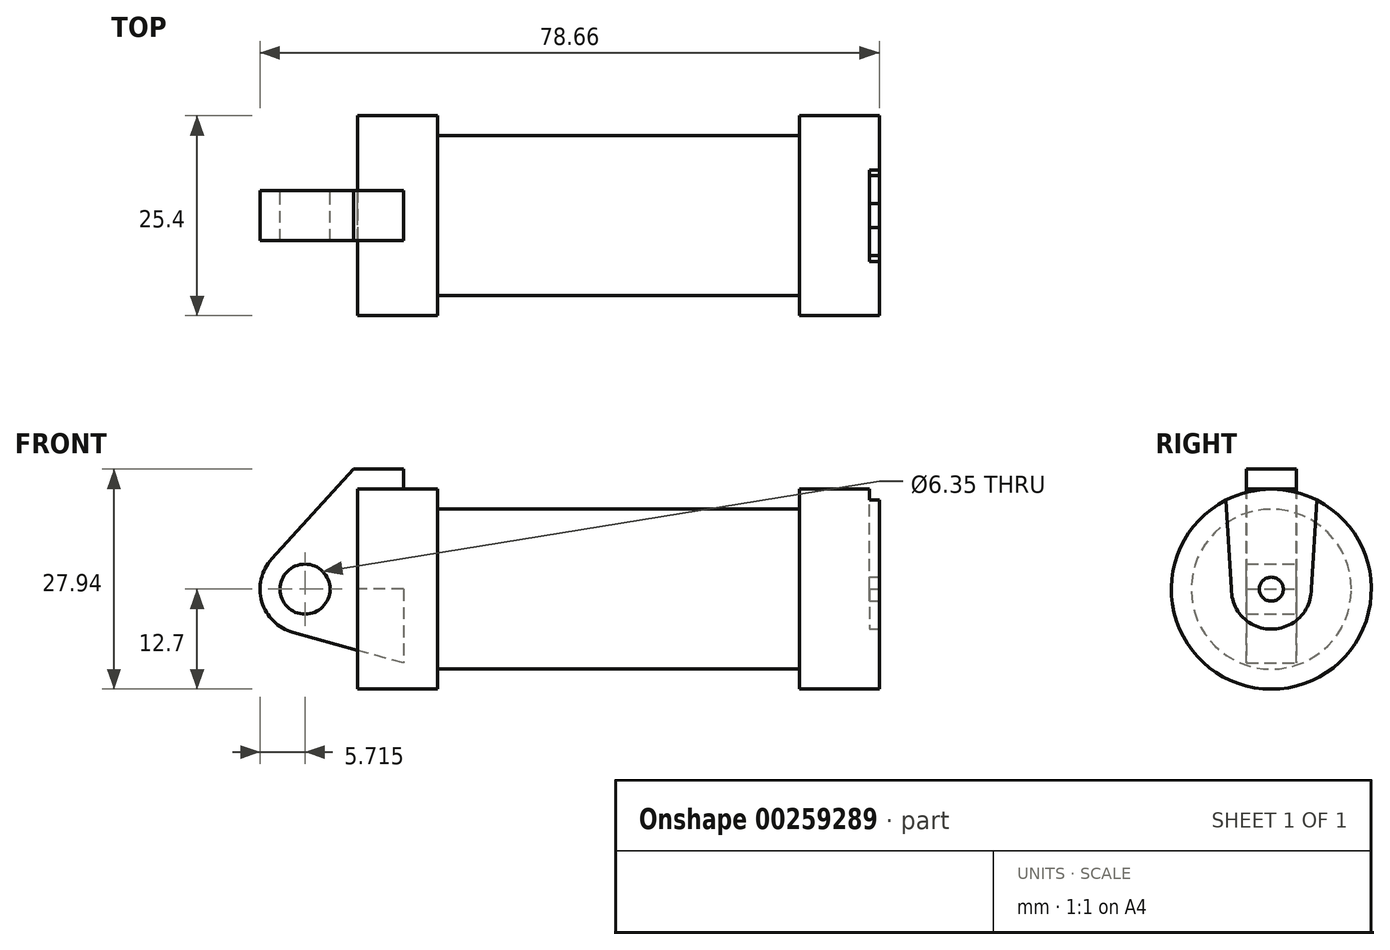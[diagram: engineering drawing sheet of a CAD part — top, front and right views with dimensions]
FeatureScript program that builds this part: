
annotation { "Feature Type Name" : "Feature", "Feature Type Description" : "" }
export const myFeature = defineFeature(function(context is Context, id is Id, definition is map)
    precondition{}
    {
        {
            var Q0;
            Q0=qCreatedBy(makeId("Front.planeOp"),FACE);
            var sketch = newSketch(context, id + "F0", { "sketchPlane" : qUnion([Q0])});
            skLineSegment(sketch, "E0", {"start": v(0, 0) * mm, "end": v(0, 12.7) * mm});
            skLineSegment(sketch, "E1", {"start": v(0, 12.7) * mm, "end": v(10.16, 12.7) * mm});
            skLineSegment(sketch, "E2", {"start": v(10.16, 12.7) * mm, "end": v(10.16, 10.16) * mm});
            skLineSegment(sketch, "E3", {"start": v(10.16, 10.16) * mm, "end": v(56.13, 10.16) * mm});
            skLineSegment(sketch, "E4", {"start": v(56.13, 10.16) * mm, "end": v(56.13, 12.7) * mm});
            skLineSegment(sketch, "E5", {"start": v(56.13, 12.7) * mm, "end": v(66.3, 12.7) * mm});
            skLineSegment(sketch, "E6", {"start": v(66.3, 12.7) * mm, "end": v(66.3, 0) * mm});
            skLineSegment(sketch, "E7", {"start": v(66.3, 0) * mm, "end": v(0, 0) * mm});
            skLineSegment(sketch, "E8", {"start": v(5.84, 15.24) * mm, "end": v(-0.5, 15.24) * mm});
            skLineSegment(sketch, "E9", {"start": v(-0.5, 15.24) * mm, "end": v(-10.88, 3.85) * mm});
            skLineSegment(sketch, "E10", {"start": v(0, 0) * mm, "end": v(-6.65, 0) * mm});
            skCircle(sketch, "E11", {"center": v(-6.65, 0) * mm, "radius": 5.72 * mm});
            skCircle(sketch, "E12", {"center": v(-6.65, 0) * mm, "radius": 3.18 * mm});
            skLineSegment(sketch, "E13", {"start": v(5.84, 15.24) * mm, "end": v(5.84, -9.4) * mm});
            skLineSegment(sketch, "E14", {"start": v(5.84, -9.4) * mm, "end": v(-8.18, -5.5) * mm});
            skSolve(sketch);
        }
        {
            var Q0;
            {var subQ3=sQuery(id+"F0.wireOp",EDGE,"E0");Q0=makeQuery(id+"F0.imprint","IMPRINT",FACE,{"disambiguationData":[TD([[makeQuery(id+"F0.imprint","IMPRINT",EDGE,{"derivedFrom":subQ3}),1.0]])]});}
            var Q1;
            {var subQ0=sQuery(id+"F0.wireOp",EDGE,"E14");Q1=makeQuery(id+"F0.imprint","IMPRINT",FACE,{"disambiguationData":[TD([[makeQuery(id+"F0.imprint","IMPRINT",EDGE,{"derivedFrom":subQ0}),-1.0]])]});}
            var Q2;
            {var subQ4=sQuery(id+"F0.wireOp",EDGE,"E12");Q2=makeQuery(id+"F0.imprint","IMPRINT",FACE,{"disambiguationData":[TD([[makeQuery(id+"F0.imprint","IMPRINT",EDGE,{"derivedFrom":subQ4}),-1.0]])]});}
            extrude(context, id + "F1", {"entities" : qUnion([Q0, Q1, Q2]), "endBound" : BoundingType.SYMMETRIC, "depth" : 6.35 * mm});
        }
        {
            var Q0;
            {var subQ0=sQuery(id+"F0.wireOp",EDGE,"E0");Q0=makeQuery(id+"F0.imprint","IMPRINT",FACE,{"disambiguationData":[TD([[makeQuery(id+"F0.imprint","IMPRINT",EDGE,{"derivedFrom":subQ0}),-1.0]])]});}
            var Q1;
            {var subQ0=sQuery(id+"F0.wireOp",EDGE,"E2");Q1=makeQuery(id+"F0.imprint","IMPRINT",FACE,{"disambiguationData":[TD([[makeQuery(id+"F0.imprint","IMPRINT",EDGE,{"derivedFrom":subQ0}),-1.0]])]});}
            var Q2;
            Q2=sQuery(id+"F0.wireOp",EDGE,"E7");
            revolve(context, id + "F2", {"entities" : qUnion([Q0, Q1]), "axis" : qUnion([Q2]), "revolveType" : RevolveType.FULL});
        }
        {
            var Q0;
            Q0=makeQuery(id+"F2.opRevolve","SWEPT_FACE",FACE,{"disambiguationData":[OSD([sQuery(id+"F0.wireOp",EDGE,"E6")])]});
            var sketch = newSketch(context, id + "F3", { "sketchPlane" : qUnion([Q0])});
            skCircle(sketch, "E15", {"center": v(0, 0) * mm, "radius": 5.08 * mm});
            skCircle(sketch, "E16", {"center": v(0, 0) * mm, "radius": 1.52 * mm});
            skLineSegment(sketch, "E17", {"start": v(-5.08, 0.03) * mm, "end": v(-6.04, 15.24) * mm});
            skLineSegment(sketch, "E18", {"start": v(5.08, 0.03) * mm, "end": v(6.04, 15.24) * mm});
            skLineSegment(sketch, "E19", {"start": v(6.04, 15.24) * mm, "end": v(-6.04, 15.24) * mm});
            skSolve(sketch);
        }
        {
            var Q0;
            {var subQ0=sQuery(id+"F3.wireOp",EDGE,"E19");Q0=makeQuery(id+"F3.imprint","IMPRINT",FACE,{"disambiguationData":[TD([[makeQuery(id+"F3.imprint","IMPRINT",EDGE,{"derivedFrom":subQ0}),1.0]])]});}
            var Q1;
            {var subQ0=sQuery(id+"F3.wireOp",EDGE,"E17");var subQ1=sQuery(id+"F3.wireOp",EDGE,"E15");var subQ2=makeQuery(id+"F3.imprint","INTERSECT",VERTEX,{"derivedFrom":[subQ1,subQ0]});Q1=makeQuery(id+"F3.imprint","IMPRINT",FACE,{"disambiguationData":[TD([[makeQuery(id+"F3.imprint","IMPRINT",EDGE,{"disambiguationData":[TD([[subQ2,1.0]])],"derivedFrom":subQ1}),-1.0]])]});}
            var Q2;
            Q2=makeQuery(id+"F3.imprint","IMPRINT",FACE,{"disambiguationData":[TD([[makeQuery(id+"F3.imprint","IMPRINT",EDGE,{"derivedFrom":sQuery(id+"F3.wireOp",EDGE,"E16")}),-1.0]])]});
            extrude(context, id + "F4", {"entities" : qUnion([Q0, Q1, Q2]), "operationType" : NewBodyOperationType.REMOVE, "oppositeDirection" : true, "depth" : 1.27 * mm});
        }
    });
